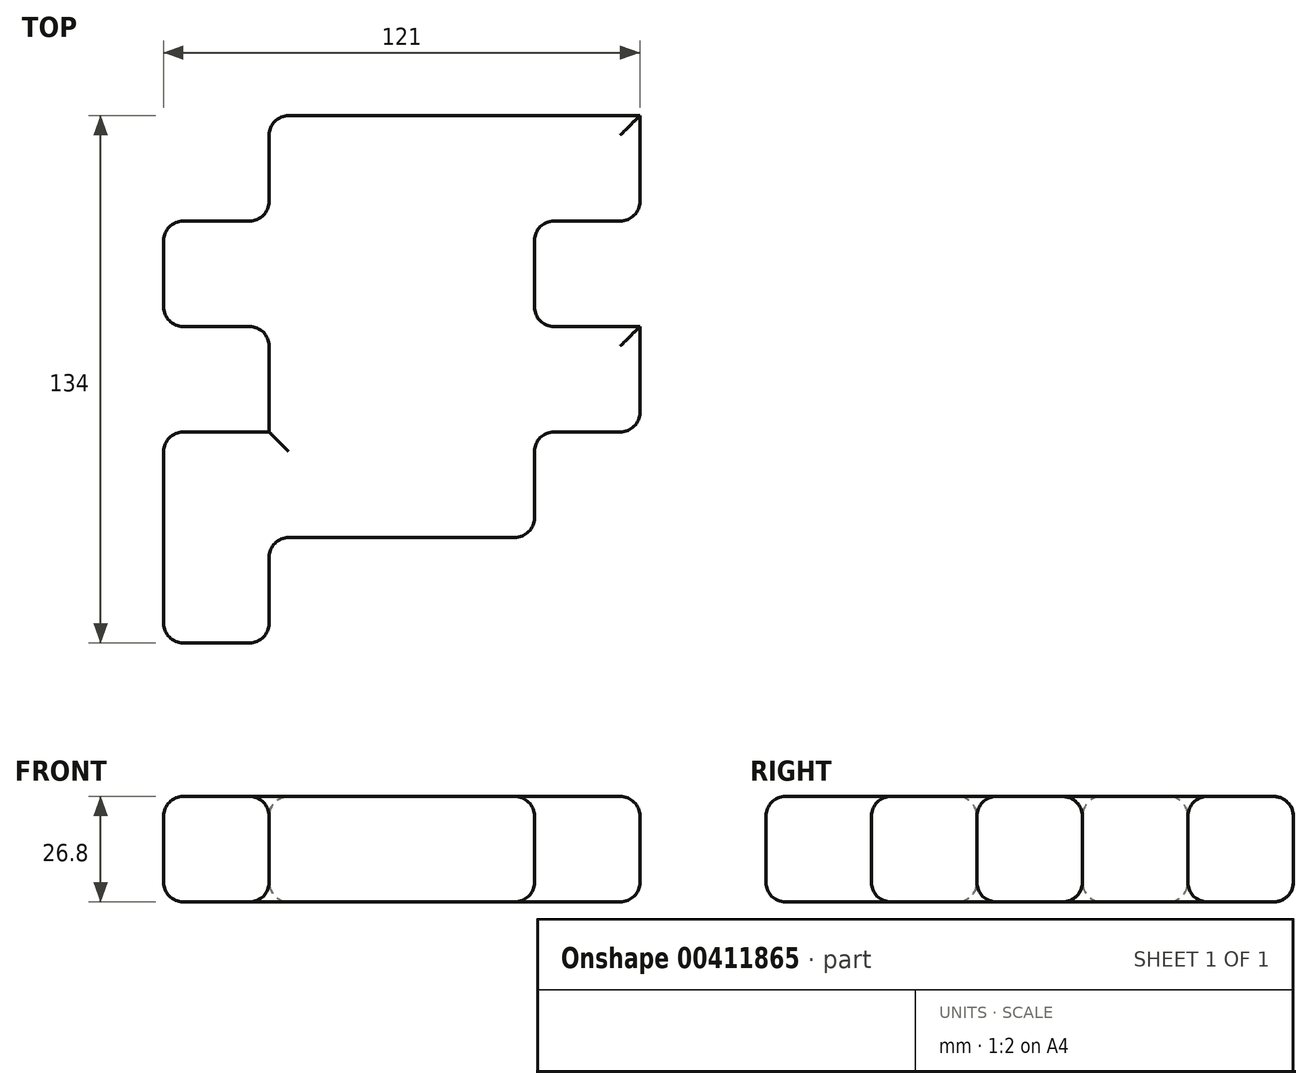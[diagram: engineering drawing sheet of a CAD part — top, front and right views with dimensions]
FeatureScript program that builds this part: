
annotation { "Feature Type Name" : "Feature", "Feature Type Description" : "" }
export const myFeature = defineFeature(function(context is Context, id is Id, definition is map)
    precondition{}
    {
        {
            var Q0;
            Q0=qCreatedBy(makeId("Top.planeOp"),FACE);
            var sketch = newSketch(context, id + "F0", { "sketchPlane" : qUnion([Q0])});
            skLineSegment(sketch, "E0.bottom", {"start": v(-64.52, 92.9) * mm, "end": v(56.48, 92.9) * mm});
            skLineSegment(sketch, "E0.top", {"start": v(-64.52, -41.1) * mm, "end": v(56.48, -41.1) * mm});
            skLineSegment(sketch, "E0.left", {"start": v(-64.52, 66.1) * mm, "end": v(-64.52, -41.1) * mm});
            skLineSegment(sketch, "E0.right", {"start": v(56.48, 92.9) * mm, "end": v(56.48, -14.3) * mm});
            skLineSegment(sketch, "E1.top", {"start": v(56.48, 66.1) * mm, "end": v(29.68, 66.1) * mm});
            skLineSegment(sketch, "E2.top", {"start": v(29.68, 39.3) * mm, "end": v(56.48, 39.3) * mm});
            skLineSegment(sketch, "E2.left", {"start": v(29.68, 66.1) * mm, "end": v(29.68, 39.3) * mm});
            skLineSegment(sketch, "E3.top", {"start": v(56.48, 12.5) * mm, "end": v(29.68, 12.5) * mm});
            skLineSegment(sketch, "E4.right", {"start": v(29.68, 12.5) * mm, "end": v(29.68, -14.3) * mm});
            skLineSegment(sketch, "E5.bottom", {"start": v(29.68, -14.3) * mm, "end": v(-37.72, -14.3) * mm});
            skLineSegment(sketch, "E5.left", {"start": v(56.48, -14.3) * mm, "end": v(56.48, -41.1) * mm});
            skLineSegment(sketch, "E5.right", {"start": v(-37.72, -14.3) * mm, "end": v(-37.72, -41.1) * mm});
            skLineSegment(sketch, "E6.top", {"start": v(-64.52, 66.1) * mm, "end": v(-37.72, 66.1) * mm});
            skLineSegment(sketch, "E6.left", {"start": v(-64.52, 92.9) * mm, "end": v(-64.52, 66.1) * mm});
            skLineSegment(sketch, "E6.right", {"start": v(-37.72, 92.9) * mm, "end": v(-37.72, 66.1) * mm});
            skLineSegment(sketch, "E7.top", {"start": v(-64.52, 39.3) * mm, "end": v(-37.72, 39.3) * mm});
            skLineSegment(sketch, "E8.top", {"start": v(-64.52, 12.5) * mm, "end": v(-37.72, 12.5) * mm});
            skLineSegment(sketch, "E8.right", {"start": v(-37.72, 39.3) * mm, "end": v(-37.72, 12.5) * mm});
            skSolve(sketch);
        }
        {
            var Q0;
            {var subQ1=sQuery(id+"F0.wireOp",EDGE,"E1.top");Q0=makeQuery(id+"F0.imprint","IMPRINT",FACE,{"disambiguationData":[TD([[makeQuery(id+"F0.imprint","IMPRINT",EDGE,{"derivedFrom":subQ1}),-1.0]])]});}
            extrude(context, id + "F1", {"entities" : qUnion([Q0]), "depth" : 26.8 * mm});
        }
        {
            var Q0;
            Q0=makeQuery(id+"F1.opExtrude","CAP_FACE",FACE,{"disambiguationData":[OSD([sQuery(id+"F0.wireOp",EDGE,"E0.bottom"),sQuery(id+"F0.wireOp",EDGE,"E0.top"),sQuery(id+"F0.wireOp",EDGE,"E0.left"),sQuery(id+"F0.wireOp",EDGE,"E0.right"),sQuery(id+"F0.wireOp",EDGE,"E1.top"),sQuery(id+"F0.wireOp",EDGE,"E2.top"),sQuery(id+"F0.wireOp",EDGE,"E2.left"),sQuery(id+"F0.wireOp",EDGE,"E3.top"),sQuery(id+"F0.wireOp",EDGE,"E4.right"),sQuery(id+"F0.wireOp",EDGE,"E5.bottom"),sQuery(id+"F0.wireOp",EDGE,"E5.right"),sQuery(id+"F0.wireOp",EDGE,"E6.top"),sQuery(id+"F0.wireOp",EDGE,"E6.right"),sQuery(id+"F0.wireOp",EDGE,"E7.top"),sQuery(id+"F0.wireOp",EDGE,"E8.top"),sQuery(id+"F0.wireOp",EDGE,"E8.right")])],"isStart":false});
            var Q1;
            Q1=makeQuery(id+"F1.opExtrude","SWEPT_FACE",FACE,{"disambiguationData":[OSD([sQuery(id+"F0.wireOp",EDGE,"E5.bottom")])]});
            var Q2;
            Q2=makeQuery(id+"F1.opExtrude","SWEPT_FACE",FACE,{"disambiguationData":[OSD([sQuery(id+"F0.wireOp",EDGE,"E5.right")])]});
            var Q3;
            Q3=makeQuery(id+"F1.opExtrude","SWEPT_FACE",FACE,{"disambiguationData":[OSD([sQuery(id+"F0.wireOp",EDGE,"E0.top")])]});
            var Q4;
            Q4=makeQuery(id+"F1.opExtrude","SWEPT_FACE",FACE,{"disambiguationData":[OSD([sQuery(id+"F0.wireOp",EDGE,"E4.right")])]});
            var Q5;
            Q5=makeQuery(id+"F1.opExtrude","SWEPT_FACE",FACE,{"disambiguationData":[OSD([sQuery(id+"F0.wireOp",EDGE,"E3.top")])]});
            var Q6;
            Q6=makeQuery(id+"F1.opExtrude","SWEPT_FACE",FACE,{"disambiguationData":[OSD([sQuery(id+"F0.wireOp",EDGE,"E1.top")])]});
            var Q7;
            Q7=makeQuery(id+"F1.opExtrude","SWEPT_FACE",FACE,{"disambiguationData":[OSD([sQuery(id+"F0.wireOp",EDGE,"E2.left")])]});
            var Q8;
            {var subQ0=sQuery(id+"F0.wireOp",EDGE,"E0.left");Q8=makeQuery(id+"F1.opExtrude","SWEPT_FACE",FACE,{"disambiguationData":[OSD([subQ0]),TDD([makeQuery(id+"F0.imprint","IMPRINT",EDGE,{"disambiguationData":[TD([[makeQuery(id+"F0.imprint","INTERSECT",VERTEX,{"derivedFrom":[sQuery(id+"F0.wireOp",EDGE,"E0.top"),subQ0]}),1.0]])],"derivedFrom":subQ0})])]});}
            var Q9;
            Q9=makeQuery(id+"F1.opExtrude","SWEPT_FACE",FACE,{"disambiguationData":[OSD([sQuery(id+"F0.wireOp",EDGE,"E7.top")])]});
            var Q10;
            Q10=makeQuery(id+"F1.opExtrude","SWEPT_EDGE",EDGE,{"disambiguationData":[OSD([sQuery(id+"F0.wireOp",EDGE,"E0.left"),sQuery(id+"F0.wireOp",EDGE,"E6.top"),sQuery(id+"F0.wireOp",EDGE,"E6.left")])]});
            var Q11;
            Q11=makeQuery(id+"F1.opExtrude","SWEPT_FACE",FACE,{"disambiguationData":[OSD([sQuery(id+"F0.wireOp",EDGE,"E6.right")])]});
            var Q12;
            Q12=makeQuery(id+"F1.opExtrude","CAP_FACE",FACE,{"disambiguationData":[OSD([sQuery(id+"F0.wireOp",EDGE,"E0.bottom"),sQuery(id+"F0.wireOp",EDGE,"E0.top"),sQuery(id+"F0.wireOp",EDGE,"E0.left"),sQuery(id+"F0.wireOp",EDGE,"E0.right"),sQuery(id+"F0.wireOp",EDGE,"E1.top"),sQuery(id+"F0.wireOp",EDGE,"E2.top"),sQuery(id+"F0.wireOp",EDGE,"E2.left"),sQuery(id+"F0.wireOp",EDGE,"E3.top"),sQuery(id+"F0.wireOp",EDGE,"E4.right"),sQuery(id+"F0.wireOp",EDGE,"E5.bottom"),sQuery(id+"F0.wireOp",EDGE,"E5.right"),sQuery(id+"F0.wireOp",EDGE,"E6.top"),sQuery(id+"F0.wireOp",EDGE,"E6.right"),sQuery(id+"F0.wireOp",EDGE,"E7.top"),sQuery(id+"F0.wireOp",EDGE,"E8.top"),sQuery(id+"F0.wireOp",EDGE,"E8.right")])],"isStart":true});
            fillet(context, id + "F2", {"entities" : qUnion([Q0, Q1, Q2, Q3, Q4, Q5, Q6, Q7, Q8, Q9, Q10, Q11, Q12]), "radius" : 5 * mm, "tangentPropagation" : true, "allowEdgeOverflow" : false});
        }
    });
